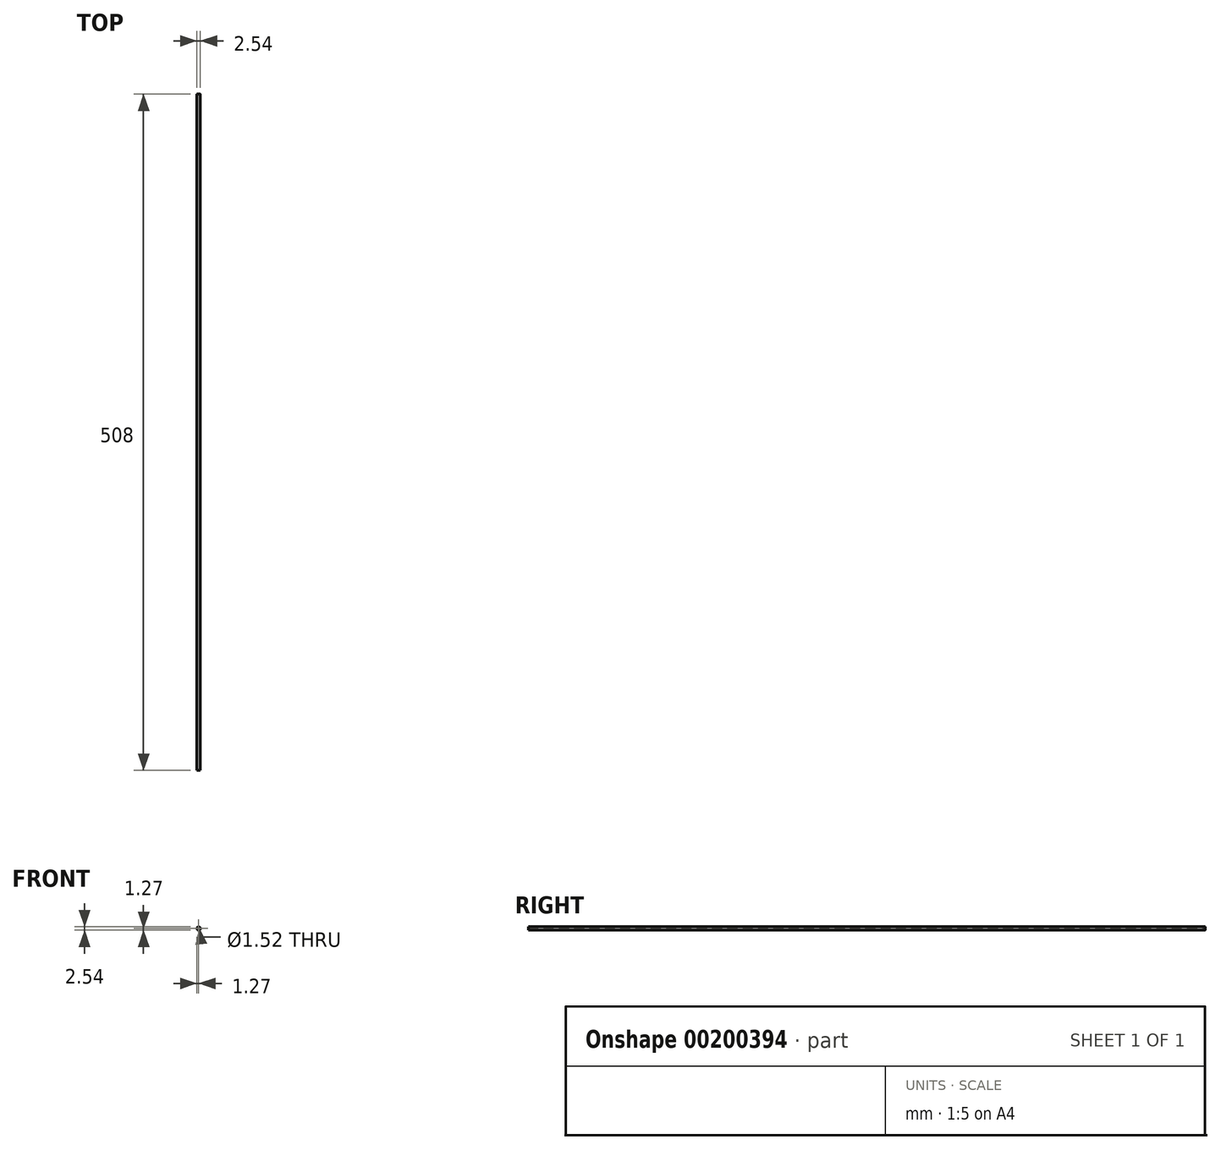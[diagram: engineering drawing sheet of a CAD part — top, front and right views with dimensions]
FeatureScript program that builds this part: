
annotation { "Feature Type Name" : "Feature", "Feature Type Description" : "" }
export const myFeature = defineFeature(function(context is Context, id is Id, definition is map)
    precondition{}
    {
        {
            var Q0;
            Q0=qCreatedBy(makeId("Front.planeOp"),FACE);
            var sketch = newSketch(context, id + "F0", { "sketchPlane" : qUnion([Q0])});
            skCircle(sketch, "E0", {"center": v(0, 0) * mm, "radius": 0.76 * mm});
            skCircle(sketch, "E1", {"center": v(0, 0) * mm, "radius": 1.27 * mm});
            skSolve(sketch);
        }
        {
            var Q0;
            Q0=makeQuery(id+"F0.imprint","IMPRINT",FACE,{"disambiguationData":[TD([[makeQuery(id+"F0.imprint","IMPRINT",EDGE,{"derivedFrom":sQuery(id+"F0.wireOp",EDGE,"E0")}),-1.0]])]});
            extrude(context, id + "F1", {"entities" : qUnion([Q0]), "depth" : 508 * mm});
        }
        {
            var Q0;
            Q0=makeQuery(id+"F1.opExtrude","CAP_EDGE",EDGE,{"disambiguationData":[OSD([sQuery(id+"F0.wireOp",EDGE,"E0")])],"isStart":true});
            chamfer(context, id + "F2", {"entities" : qUnion([Q0]), "width" : 0.25 * mm, "tangentPropagation" : true});
        }
        {
            var Q0;
            Q0=makeQuery(id+"F1.opExtrude","CAP_EDGE",EDGE,{"disambiguationData":[OSD([sQuery(id+"F0.wireOp",EDGE,"E1")])],"isStart":true});
            fillet(context, id + "F3", {"entities" : qUnion([Q0]), "radius" : 0.05 * mm, "tangentPropagation" : true, "allowEdgeOverflow" : false});
        }
    });
